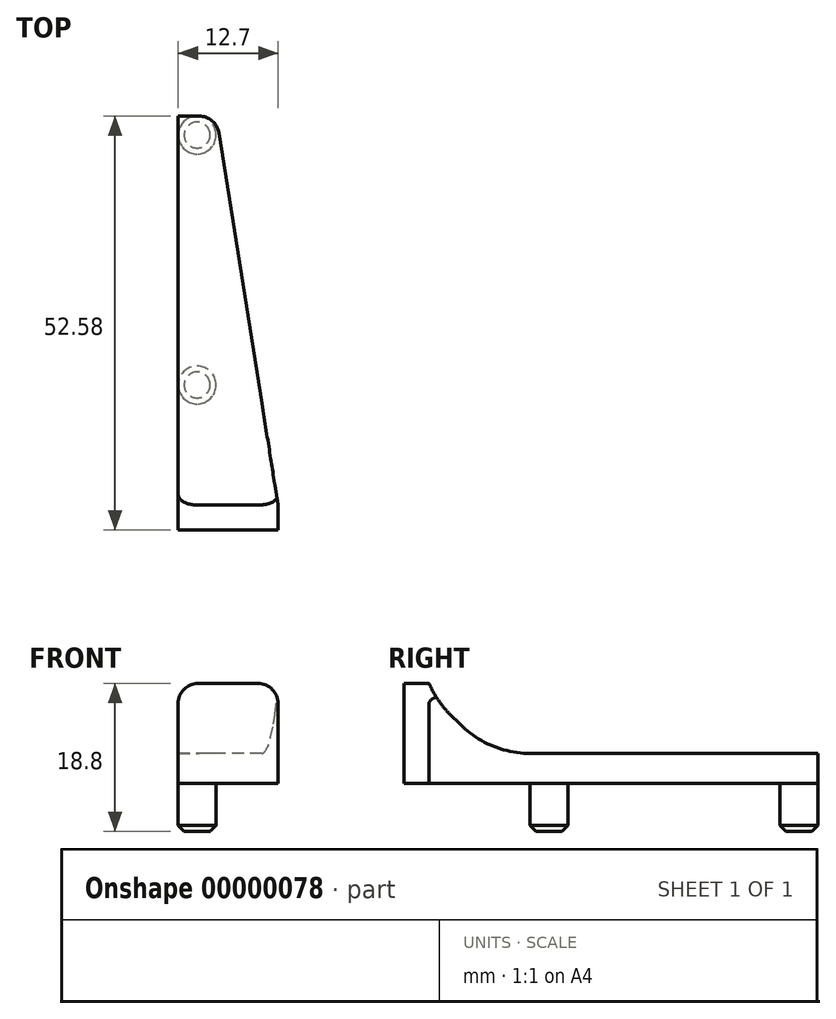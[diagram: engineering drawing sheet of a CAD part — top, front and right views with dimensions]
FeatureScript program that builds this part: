
annotation { "Feature Type Name" : "Feature", "Feature Type Description" : "" }
export const myFeature = defineFeature(function(context is Context, id is Id, definition is map)
    precondition{}
    {
        {
            var Q0;
            Q0=qCreatedBy(makeId("Top.planeOp"),FACE);
            var sketch = newSketch(context, id + "F0", { "sketchPlane" : qUnion([Q0])});
            skLineSegment(sketch, "E0.bottom", {"start": v(-2.41, 3.17) * mm, "end": v(10.29, 3.18) * mm});
            skLineSegment(sketch, "E0.top", {"start": v(-2.41, 0) * mm, "end": v(10.29, 0) * mm});
            skLineSegment(sketch, "E0.left", {"start": v(-2.41, 3.17) * mm, "end": v(-2.41, 0) * mm});
            skLineSegment(sketch, "E0.right", {"start": v(10.29, 3.17) * mm, "end": v(10.29, 0) * mm});
            skCircle(sketch, "E1", {"center": v(0, 18.42) * mm, "radius": 2.41 * mm});
            skCircle(sketch, "E2", {"center": v(0, 50.17) * mm, "radius": 2.41 * mm});
            skLineSegment(sketch, "E3", {"start": v(-2.41, 3.17) * mm, "end": v(-2.41, 52.58) * mm});
            skLineSegment(sketch, "E4.MirrorCS", {"start": v(10.29, 3.17) * mm, "end": v(2.41, 52.58) * mm});
            skLineSegment(sketch, "E5", {"start": v(-2.41, 52.58) * mm, "end": v(2.41, 52.58) * mm});
            skLineSegment(sketch, "E6", {"start": v(0, 52.58) * mm, "end": v(0, 0) * mm, "construction": true});
            skSolve(sketch);
        }
        {
            var Q0;
            Q0 = qSketchRegion(id + "F0", true);
            extrude(context, id + "F1", {"entities" : qUnion([Q0]), "depth" : 3.8 * mm});
        }
        {
            var Q0;
            Q0=makeQuery(id+"F0.imprint","IMPRINT",FACE,{"disambiguationData":[TD([[makeQuery(id+"F0.imprint","IMPRINT",EDGE,{"derivedFrom":sQuery(id+"F0.wireOp",EDGE,"E0.bottom")}),-1.0]])]});
            extrude(context, id + "F2", {"entities" : qUnion([Q0]), "operationType" : NewBodyOperationType.ADD, "depth" : 12.7 * mm});
        }
        {
            var Q0;
            Q0=makeQuery(id+"F0.imprint","IMPRINT",FACE,{"disambiguationData":[TD([[makeQuery(id+"F0.imprint","IMPRINT",EDGE,{"derivedFrom":sQuery(id+"F0.wireOp",EDGE,"E1")}),1.0]])]});
            var Q1;
            {var subQ0=sQuery(id+"F0.wireOp",EDGE,"E2");var subQ1=makeQuery(id+"F0.imprint","INTERSECT",VERTEX,{"derivedFrom":[subQ0,sQuery(id+"F0.wireOp",EDGE,"E3")]});Q1=makeQuery(id+"F0.imprint","IMPRINT",FACE,{"disambiguationData":[TD([[makeQuery(id+"F0.imprint","IMPRINT",EDGE,{"disambiguationData":[TD([[subQ1,1.0]])],"derivedFrom":subQ0}),1.0]])]});}
            extrude(context, id + "F3", {"entities" : qUnion([Q0, Q1]), "operationType" : NewBodyOperationType.ADD, "oppositeDirection" : true, "depth" : 6.1 * mm});
        }
        {
            var Q0;
            Q0=makeQuery(id+"F3.opExtrude","CAP_EDGE",EDGE,{"disambiguationData":[OSD([sQuery(id+"F0.wireOp",EDGE,"E1")])],"isStart":false});
            var Q1;
            Q1=makeQuery(id+"F3.opExtrude","CAP_EDGE",EDGE,{"disambiguationData":[OSD([sQuery(id+"F0.wireOp",EDGE,"E2")])],"isStart":false});
            chamfer(context, id + "F4", {"entities" : qUnion([Q0, Q1]), "width" : 0.76 * mm, "tangentPropagation" : true});
        }
        {
            var Q0;
            Q0=makeQuery(id+"F2.boolean.opBoolean","INTERSECT",EDGE,{"derivedFrom":[makeQuery(id+"F1.opExtrude","CAP_FACE",FACE,{"disambiguationData":[OSD([sQuery(id+"F0.wireOp",EDGE,"E0.top"),sQuery(id+"F0.wireOp",EDGE,"E0.left"),sQuery(id+"F0.wireOp",EDGE,"E0.right"),sQuery(id+"F0.wireOp",EDGE,"E3"),sQuery(id+"F0.wireOp",EDGE,"E4.MirrorCS"),sQuery(id+"F0.wireOp",EDGE,"E5")])],"isStart":false}),makeQuery(id+"F2.opExtrude","SWEPT_FACE",FACE,{"disambiguationData":[OSD([sQuery(id+"F0.wireOp",EDGE,"E0.bottom")])]})]});
            chamfer(context, id + "F5", {"entities" : qUnion([Q0]), "width" : 7.62 * mm, "tangentPropagation" : true});
        }
        {
            var Q0;
            {var subQ0=makeQuery(id+"F2.opExtrude","SWEPT_FACE",FACE,{"disambiguationData":[OSD([sQuery(id+"F0.wireOp",EDGE,"E0.bottom")])]});Q0=makeQuery(id+"F5.opChamfer","BLEND_EDGE",EDGE,{"blendedFrom":[makeQuery(id+"F2.boolean.opBoolean","INTERSECT",EDGE,{"derivedFrom":[makeQuery(id+"F1.opExtrude","CAP_FACE",FACE,{"disambiguationData":[OSD([sQuery(id+"F0.wireOp",EDGE,"E0.top"),sQuery(id+"F0.wireOp",EDGE,"E0.left"),sQuery(id+"F0.wireOp",EDGE,"E0.right"),sQuery(id+"F0.wireOp",EDGE,"E3"),sQuery(id+"F0.wireOp",EDGE,"E4.MirrorCS"),sQuery(id+"F0.wireOp",EDGE,"E5")])],"isStart":false}),subQ0]}),subQ0],"blendedInto":[subQ0]});}
            var Q1;
            {var subQ0=makeQuery(id+"F1.opExtrude","CAP_FACE",FACE,{"disambiguationData":[OSD([sQuery(id+"F0.wireOp",EDGE,"E0.top"),sQuery(id+"F0.wireOp",EDGE,"E0.left"),sQuery(id+"F0.wireOp",EDGE,"E0.right"),sQuery(id+"F0.wireOp",EDGE,"E3"),sQuery(id+"F0.wireOp",EDGE,"E4.MirrorCS"),sQuery(id+"F0.wireOp",EDGE,"E5")])],"isStart":false});Q1=makeQuery(id+"F5.opChamfer","BLEND_EDGE",EDGE,{"blendedFrom":[makeQuery(id+"F2.boolean.opBoolean","INTERSECT",EDGE,{"derivedFrom":[subQ0,makeQuery(id+"F2.opExtrude","SWEPT_FACE",FACE,{"disambiguationData":[OSD([sQuery(id+"F0.wireOp",EDGE,"E0.bottom")])]})]}),subQ0],"blendedInto":[subQ0]});}
            fillet(context, id + "F6", {"entities" : qUnion([Q0, Q1]), "radius" : 12.7 * mm, "tangentPropagation" : true, "allowEdgeOverflow" : false});
        }
        {
            var Q0;
            Q0=makeQuery(id+"F2.opExtrude","CAP_EDGE",EDGE,{"disambiguationData":[OSD([sQuery(id+"F0.wireOp",EDGE,"E0.right")])],"isStart":false});
            var Q1;
            Q1=makeQuery(id+"F2.opExtrude","CAP_EDGE",EDGE,{"disambiguationData":[OSD([sQuery(id+"F0.wireOp",EDGE,"E0.left")])],"isStart":false});
            fillet(context, id + "F7", {"entities" : qUnion([Q0, Q1]), "radius" : 2.54 * mm, "tangentPropagation" : true, "allowEdgeOverflow" : false});
        }
        {
            var Q0;
            Q0=makeQuery(id+"F1.opExtrude","SWEPT_EDGE",EDGE,{"disambiguationData":[OSD([sQuery(id+"F0.wireOp",EDGE,"E4.MirrorCS"),sQuery(id+"F0.wireOp",EDGE,"E5")])]});
            fillet(context, id + "F8", {"entities" : qUnion([Q0]), "radius" : 2.54 * mm, "tangentPropagation" : true, "allowEdgeOverflow" : false});
        }
    });
